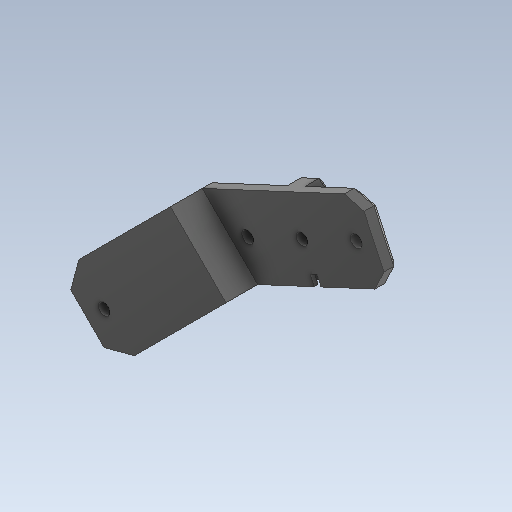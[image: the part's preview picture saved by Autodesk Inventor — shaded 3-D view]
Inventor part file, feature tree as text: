
AUTODESK INVENTOR PART (.ipt)
format: ipt  version: 2020 (Build 240168000, 168)  size: 242,688 bytes
history: native  units: in
note: dims shown in document units (in); Inventor stores cm internally (conversion verified against a paired STEP export)
features: sketch x15, other x3
ambient origin geometry x8: Origin, YZ Plane, XZ Plane, XY Plane, X Axis, Y Axis, Z Axis, Center Point
bodies: Solid1 (feature_tree)
feature tree (18):
  other  "TibiaTop.ipt"
  other  "Solid2::TibiaTop.ipt"
  other  "TaggingFeature1"
  sketch  "Sketch1"  dims[d0=0.3937in]
  sketch  "Sketch9"
  sketch  "Sketch10"
  sketch  "Sketch11"
  sketch  "Sketch15"
  sketch  "Sketch25"
  sketch  "Sketch26"
  sketch  "Sketch27"
  sketch  "Sketch29"
  sketch  "Sketch30"
  sketch  "Sketch31"
  sketch  "Sketch32"
  sketch  "Sketch34"
  sketch  "Sketch35"
  sketch  "Sketch37"
